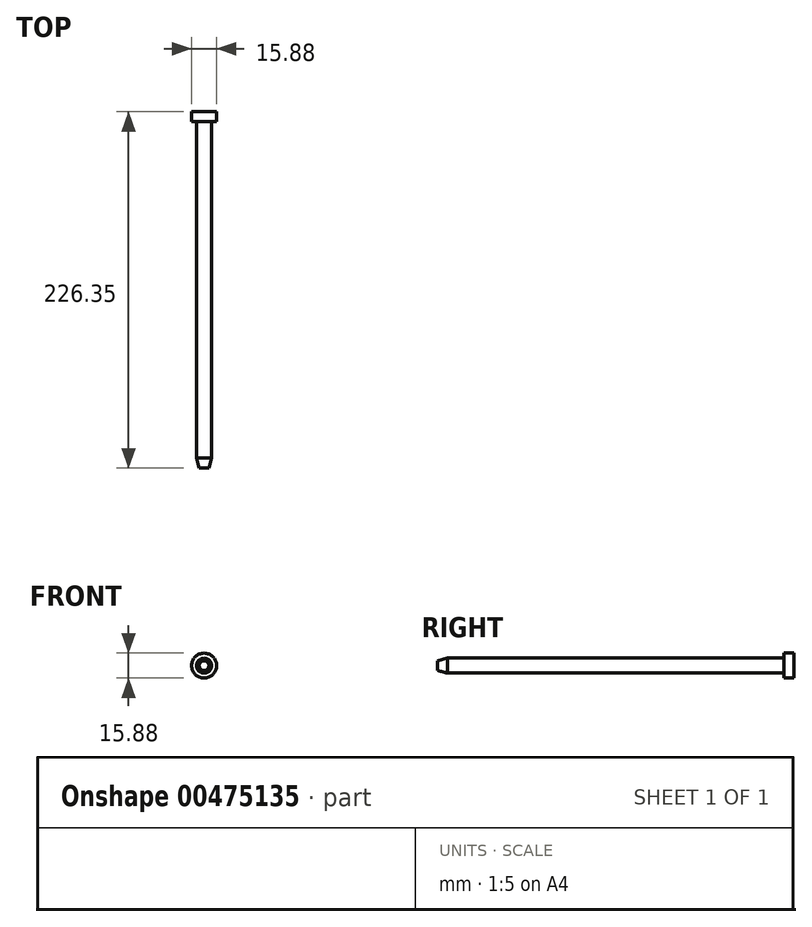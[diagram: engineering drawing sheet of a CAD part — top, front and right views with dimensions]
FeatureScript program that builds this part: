
annotation { "Feature Type Name" : "Feature", "Feature Type Description" : "" }
export const myFeature = defineFeature(function(context is Context, id is Id, definition is map)
    precondition{}
    {
        {
            var Q0;
            Q0=qCreatedBy(makeId("Right.planeOp"),FACE);
            var sketch = newSketch(context, id + "F0", { "sketchPlane" : qUnion([Q0])});
            skLineSegment(sketch, "E0", {"start": v(0, 0) * mm, "end": v(0, 7.94) * mm});
            skLineSegment(sketch, "E1", {"start": v(0, 7.94) * mm, "end": v(-6.35, 7.94) * mm});
            skLineSegment(sketch, "E2", {"start": v(-6.35, 7.94) * mm, "end": v(-6.35, 4.76) * mm});
            skLineSegment(sketch, "E3", {"start": v(-6.35, 4.76) * mm, "end": v(-220, 4.76) * mm});
            skLineSegment(sketch, "E4", {"start": v(-220, 4.76) * mm, "end": v(-226.35, 3.06) * mm});
            skLineSegment(sketch, "E5", {"start": v(-226.35, 3.06) * mm, "end": v(-226.35, 0) * mm});
            skLineSegment(sketch, "E6", {"start": v(-226.35, 0) * mm, "end": v(0, 0) * mm});
            skSolve(sketch);
        }
        {
            var Q0;
            Q0=makeQuery(id+"F0.imprint","IMPRINT",FACE,{"disambiguationData":[TD([[makeQuery(id+"F0.imprint","IMPRINT",EDGE,{"derivedFrom":sQuery(id+"F0.wireOp",EDGE,"E0")}),1.0]])]});
            var Q1;
            Q1=sQuery(id+"F0.wireOp",EDGE,"E6");
            revolve(context, id + "F1", {"entities" : qUnion([Q0]), "axis" : qUnion([Q1]), "revolveType" : RevolveType.FULL});
        }
    });
